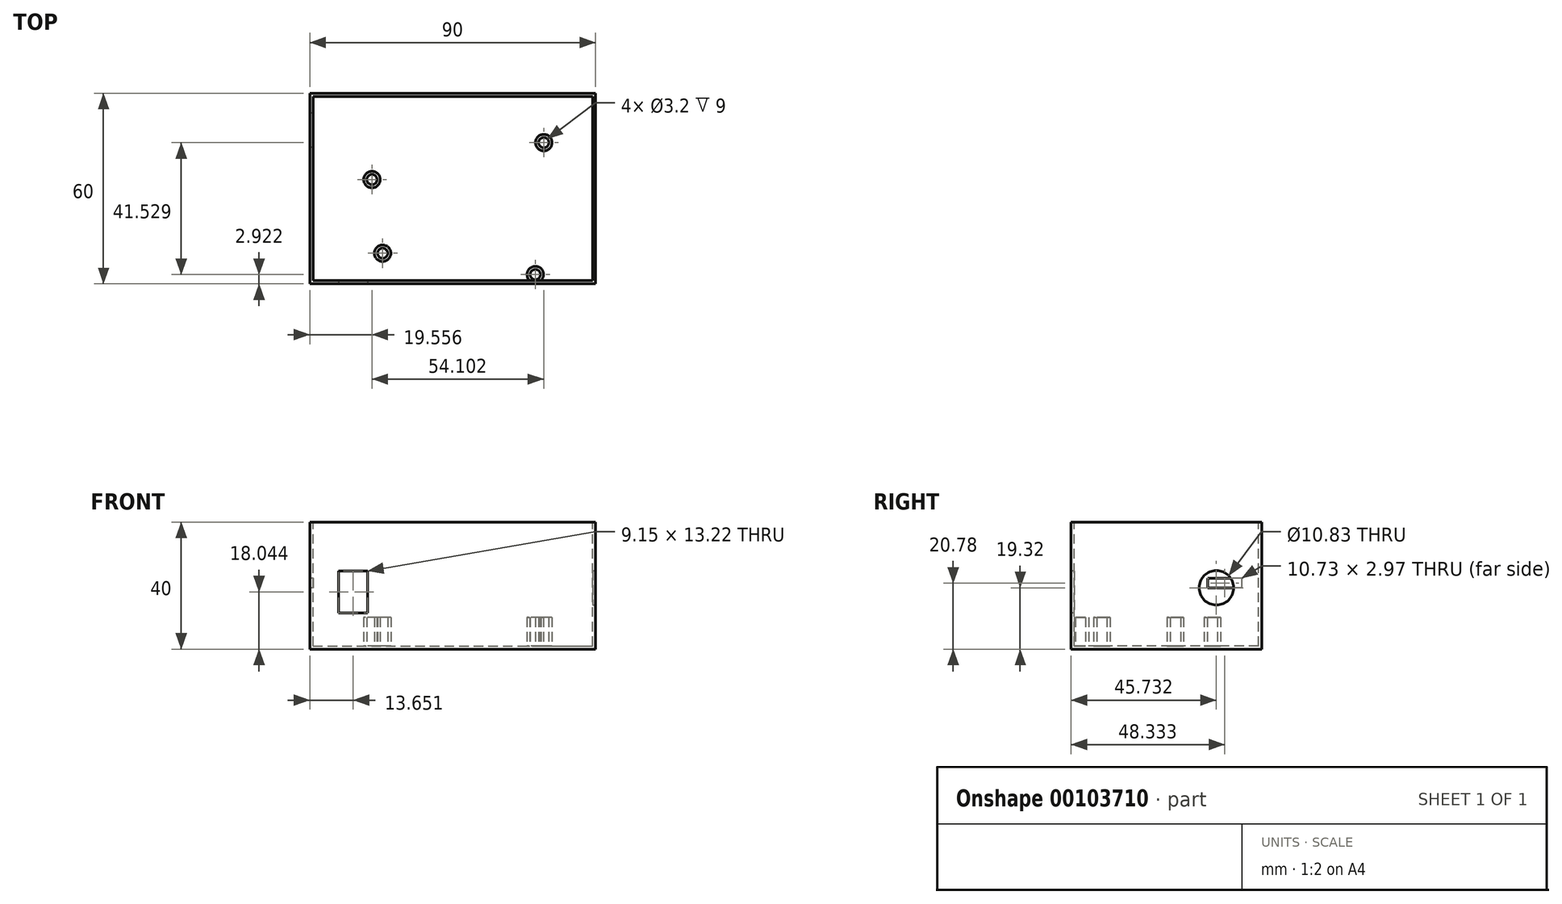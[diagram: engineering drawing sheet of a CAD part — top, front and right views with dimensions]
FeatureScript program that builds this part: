
annotation { "Feature Type Name" : "Feature", "Feature Type Description" : "" }
export const myFeature = defineFeature(function(context is Context, id is Id, definition is map)
    precondition{}
    {
        {
            var Q0;
            Q0=qCreatedBy(makeId("Top.planeOp"),FACE);
            var sketch = newSketch(context, id + "F0", { "sketchPlane" : qUnion([Q0])});
            skLineSegment(sketch, "E0.bottom", {"start": v(-37.33, 28.43) * mm, "end": v(52.67, 28.43) * mm});
            skLineSegment(sketch, "E0.top", {"start": v(-37.33, -31.57) * mm, "end": v(52.67, -31.57) * mm});
            skLineSegment(sketch, "E0.left", {"start": v(-37.33, 28.43) * mm, "end": v(-37.33, -31.57) * mm});
            skLineSegment(sketch, "E0.right", {"start": v(52.67, 28.43) * mm, "end": v(52.67, -31.57) * mm});
            skCircle(sketch, "E1", {"center": v(-14.4, -21.94) * mm, "radius": 1.6 * mm});
            skCircle(sketch, "E2", {"center": v(-17.77, 1.27) * mm, "radius": 1.6 * mm});
            skCircle(sketch, "E3", {"center": v(36.33, 12.88) * mm, "radius": 1.6 * mm});
            skCircle(sketch, "E4", {"center": v(33.66, -28.65) * mm, "radius": 1.6 * mm});
            skCircle(sketch, "E5", {"center": v(-14.4, -21.94) * mm, "radius": 2.6 * mm});
            skCircle(sketch, "E6", {"center": v(-17.77, 1.27) * mm, "radius": 2.6 * mm});
            skCircle(sketch, "E7", {"center": v(36.33, 12.88) * mm, "radius": 2.6 * mm});
            skCircle(sketch, "E8", {"center": v(33.66, -28.65) * mm, "radius": 2.6 * mm});
            skSolve(sketch);
        }
        {
            var Q0;
            Q0=makeQuery(id+"F0.imprint","IMPRINT",FACE,{"disambiguationData":[TD([[makeQuery(id+"F0.imprint","IMPRINT",EDGE,{"derivedFrom":sQuery(id+"F0.wireOp",EDGE,"E0.bottom")}),-1.0]])]});
            var Q1;
            Q1=makeQuery(id+"F0.imprint","IMPRINT",FACE,{"disambiguationData":[TD([[makeQuery(id+"F0.imprint","IMPRINT",EDGE,{"derivedFrom":sQuery(id+"F0.wireOp",EDGE,"E2")}),1.0]])]});
            var Q2;
            Q2=makeQuery(id+"F0.imprint","IMPRINT",FACE,{"disambiguationData":[TD([[makeQuery(id+"F0.imprint","IMPRINT",EDGE,{"derivedFrom":sQuery(id+"F0.wireOp",EDGE,"E2")}),-1.0]])]});
            var Q3;
            Q3=makeQuery(id+"F0.imprint","IMPRINT",FACE,{"disambiguationData":[TD([[makeQuery(id+"F0.imprint","IMPRINT",EDGE,{"derivedFrom":sQuery(id+"F0.wireOp",EDGE,"E1")}),-1.0]])]});
            var Q4;
            Q4=makeQuery(id+"F0.imprint","IMPRINT",FACE,{"disambiguationData":[TD([[makeQuery(id+"F0.imprint","IMPRINT",EDGE,{"derivedFrom":sQuery(id+"F0.wireOp",EDGE,"E1")}),1.0]])]});
            var Q5;
            Q5=makeQuery(id+"F0.imprint","IMPRINT",FACE,{"disambiguationData":[TD([[makeQuery(id+"F0.imprint","IMPRINT",EDGE,{"derivedFrom":sQuery(id+"F0.wireOp",EDGE,"E4")}),-1.0]])]});
            var Q6;
            Q6=makeQuery(id+"F0.imprint","IMPRINT",FACE,{"disambiguationData":[TD([[makeQuery(id+"F0.imprint","IMPRINT",EDGE,{"derivedFrom":sQuery(id+"F0.wireOp",EDGE,"E4")}),1.0]])]});
            var Q7;
            Q7=makeQuery(id+"F0.imprint","IMPRINT",FACE,{"disambiguationData":[TD([[makeQuery(id+"F0.imprint","IMPRINT",EDGE,{"derivedFrom":sQuery(id+"F0.wireOp",EDGE,"E3")}),-1.0]])]});
            var Q8;
            Q8=makeQuery(id+"F0.imprint","IMPRINT",FACE,{"disambiguationData":[TD([[makeQuery(id+"F0.imprint","IMPRINT",EDGE,{"derivedFrom":sQuery(id+"F0.wireOp",EDGE,"E3")}),1.0]])]});
            extrude(context, id + "F1", {"entities" : qUnion([Q0, Q1, Q2, Q3, Q4, Q5, Q6, Q7, Q8]), "depth" : 40 * mm});
        }
        {
            var Q0;
            Q0=makeQuery(id+"F1.opExtrude","CAP_FACE",FACE,{"disambiguationData":[OSD([sQuery(id+"F0.wireOp",EDGE,"E0.bottom"),sQuery(id+"F0.wireOp",EDGE,"E0.top"),sQuery(id+"F0.wireOp",EDGE,"E0.left"),sQuery(id+"F0.wireOp",EDGE,"E0.right"),sQuery(id+"F0.wireOp",EDGE,"E5"),sQuery(id+"F0.wireOp",EDGE,"E6"),sQuery(id+"F0.wireOp",EDGE,"E7"),sQuery(id+"F0.wireOp",EDGE,"E8")])],"isStart":false});
            var sketch = newSketch(context, id + "F2", { "sketchPlane" : qUnion([Q0])});
            skLineSegment(sketch, "E9.bottom", {"start": v(-36.33, 27.43) * mm, "end": v(51.67, 27.43) * mm});
            skLineSegment(sketch, "E9.top", {"start": v(-36.33, -30.57) * mm, "end": v(51.67, -30.57) * mm});
            skLineSegment(sketch, "E9.left", {"start": v(-36.33, 27.43) * mm, "end": v(-36.33, -30.57) * mm});
            skLineSegment(sketch, "E9.right", {"start": v(51.67, 27.43) * mm, "end": v(51.67, -30.57) * mm});
            skSolve(sketch);
        }
        {
            var Q0;
            Q0=makeQuery(id+"F2.imprint","IMPRINT",FACE,{"disambiguationData":[TD([[makeQuery(id+"F2.imprint","IMPRINT",EDGE,{"derivedFrom":sQuery(id+"F2.wireOp",EDGE,"E9.bottom")}),-1.0]])]});
            extrude(context, id + "F3", {"entities" : qUnion([Q0]), "operationType" : NewBodyOperationType.REMOVE, "oppositeDirection" : true, "depth" : 39 * mm});
        }
        {
            var Q0;
            Q0=makeQuery(id+"F0.imprint","IMPRINT",FACE,{"disambiguationData":[TD([[makeQuery(id+"F0.imprint","IMPRINT",EDGE,{"derivedFrom":sQuery(id+"F0.wireOp",EDGE,"E1")}),-1.0]])]});
            var Q1;
            Q1=makeQuery(id+"F0.imprint","IMPRINT",FACE,{"disambiguationData":[TD([[makeQuery(id+"F0.imprint","IMPRINT",EDGE,{"derivedFrom":sQuery(id+"F0.wireOp",EDGE,"E2")}),-1.0]])]});
            var Q2;
            Q2=makeQuery(id+"F0.imprint","IMPRINT",FACE,{"disambiguationData":[TD([[makeQuery(id+"F0.imprint","IMPRINT",EDGE,{"derivedFrom":sQuery(id+"F0.wireOp",EDGE,"E4")}),-1.0]])]});
            var Q3;
            Q3=makeQuery(id+"F0.imprint","IMPRINT",FACE,{"disambiguationData":[TD([[makeQuery(id+"F0.imprint","IMPRINT",EDGE,{"derivedFrom":sQuery(id+"F0.wireOp",EDGE,"E3")}),-1.0]])]});
            extrude(context, id + "F4", {"entities" : qUnion([Q0, Q1, Q2, Q3]), "operationType" : NewBodyOperationType.ADD, "depth" : 10 * mm});
        }
        {
            var Q0;
            Q0=makeQuery(id+"F1.opExtrude","SWEPT_FACE",FACE,{"disambiguationData":[OSD([sQuery(id+"F0.wireOp",EDGE,"E0.top")])]});
            var sketch = newSketch(context, id + "F5", { "sketchPlane" : qUnion([Q0])});
            skLineSegment(sketch, "E10.bottom", {"start": v(-28.25, 24.65) * mm, "end": v(-19.1, 24.65) * mm});
            skLineSegment(sketch, "E10.top", {"start": v(-28.25, 11.43) * mm, "end": v(-19.1, 11.43) * mm});
            skLineSegment(sketch, "E10.left", {"start": v(-28.25, 24.65) * mm, "end": v(-28.25, 11.43) * mm});
            skLineSegment(sketch, "E10.right", {"start": v(-19.1, 24.65) * mm, "end": v(-19.1, 11.43) * mm});
            skSolve(sketch);
        }
        {
            var Q0;
            Q0=makeQuery(id+"F5.imprint","IMPRINT",FACE,{"disambiguationData":[TD([[makeQuery(id+"F5.imprint","IMPRINT",EDGE,{"derivedFrom":sQuery(id+"F5.wireOp",EDGE,"E10.bottom")}),-1.0]])]});
            extrude(context, id + "F6", {"entities" : qUnion([Q0]), "operationType" : NewBodyOperationType.REMOVE, "oppositeDirection" : true, "depth" : 2 * mm});
        }
        {
            var Q0;
            Q0=makeQuery(id+"F1.opExtrude","SWEPT_FACE",FACE,{"disambiguationData":[OSD([sQuery(id+"F0.wireOp",EDGE,"E0.left")])]});
            var sketch = newSketch(context, id + "F7", { "sketchPlane" : qUnion([Q0])});
            skLineSegment(sketch, "E11.bottom", {"start": v(-22.13, 22.26) * mm, "end": v(-11.4, 22.26) * mm});
            skLineSegment(sketch, "E11.top", {"start": v(-22.13, 19.3) * mm, "end": v(-11.4, 19.3) * mm});
            skLineSegment(sketch, "E11.left", {"start": v(-22.13, 22.26) * mm, "end": v(-22.13, 19.3) * mm});
            skLineSegment(sketch, "E11.right", {"start": v(-11.4, 22.26) * mm, "end": v(-11.4, 19.3) * mm});
            skSolve(sketch);
        }
        {
            var Q0;
            Q0=makeQuery(id+"F7.imprint","IMPRINT",FACE,{"disambiguationData":[TD([[makeQuery(id+"F7.imprint","IMPRINT",EDGE,{"derivedFrom":sQuery(id+"F7.wireOp",EDGE,"E11.bottom")}),-1.0]])]});
            extrude(context, id + "F8", {"entities" : qUnion([Q0]), "operationType" : NewBodyOperationType.REMOVE, "oppositeDirection" : true, "depth" : 2 * mm});
        }
        {
            var Q0;
            Q0=makeQuery(id+"F1.opExtrude","SWEPT_FACE",FACE,{"disambiguationData":[OSD([sQuery(id+"F0.wireOp",EDGE,"E0.right")])]});
            var sketch = newSketch(context, id + "F9", { "sketchPlane" : qUnion([Q0])});
            skCircle(sketch, "E12", {"center": v(14.16, 19.32) * mm, "radius": 5.41 * mm});
            skSolve(sketch);
        }
        {
            var Q0;
            Q0=makeQuery(id+"F9.imprint","IMPRINT",FACE,{"disambiguationData":[TD([[makeQuery(id+"F9.imprint","IMPRINT",EDGE,{"derivedFrom":sQuery(id+"F9.wireOp",EDGE,"E12")}),1.0]])]});
            extrude(context, id + "F10", {"entities" : qUnion([Q0]), "operationType" : NewBodyOperationType.REMOVE, "oppositeDirection" : true, "depth" : 2 * mm});
        }
    });
